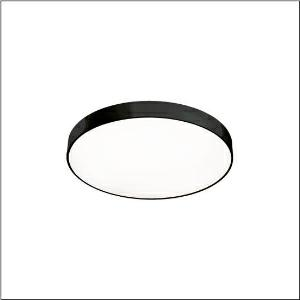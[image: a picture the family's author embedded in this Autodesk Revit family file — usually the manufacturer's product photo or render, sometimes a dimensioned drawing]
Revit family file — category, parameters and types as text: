
# Revit family: round_21_m_51mr36fm8421b
name_source: partatom
category: Lighting Fixtures
units: mm (PartAtom-declared; Revit-internal decimal feet)

## family parameters
Cut with Voids When Loaded = No
Host = Face
Light Source = No
Part Type = Normal
Room Calculation Point = No
Round Connector Dimension = Use Diameter
Shared = No

## types (1)
- --- (1 x LED, 8140 lm, 61.1 W, 4000K)
    Apparent Load = 61 VA
    CIE Flux Codes = 49 80 96 100 100
    Color Rendering = 80
    Color Temperature = 4000K
    Default Elevation = 1800 mm
    Description = Round 21 M, wall and ceiling luminaire, primary optical cover: cover, of PMMA, opal, light emission: direct distribution, primary light characteristic: symmetric, installation type: surface-mounted, suspended mounting, LED, rated luminous flux: 8.140lm, luminous efficacy: 133lm/W, light colour: 840, colour temperature: 4000K, with terminal, 3-pole, mains connection: 230V, AC, 50/60Hz, rated input power: 61W, housing, of aluminium, coated, black, diameter: 600mm, height: 62mm, protection rating (complete): IP40, insulation class (complete): insulation class I (protective earthing), certification: CE, impact resistance: IK04, permissible operating ambient temperature: -10..+35°C, packaging unit: 1 piece
    Height = 87 mm
    Lamp = 1 x LED
    Lamp Light Flux = 8140 lm
    Lamp Power = 61.1 W
    Lamp count = 1
    Length = 600 mm
    Luminous efficacy = 133 lm/W
    Manufacturer = Siteco
    ModVariant = No
    Model = 51MR36FM8421B
    Mounting Place = Ceiling
    Mounting Type = Surface mounted
    Number of Poles = 1
    OnlyDefault = Yes
    Power Factor = 1
    Product Name = Round 21 M
    Product group = wall and ceiling luminaire
    ProductGroupID = 301
    Protection Class = Protection class I
    Protection Degree = IP 40
    RLX_Detail_Level = 1
    RLX_Emergency_Light_Flux = 0 lm
    RLX_Emergency_Type = 0
    RLX_Emergency_Type_DB = No
    RlxData = <blob elided: 20321 chars, md5=0edd09dc>
    Socket = socket
    Standby Power = 0 W
    System Light Flux = 8140 lm
    System Power = 61 W
    Type Comments = factory setting: luminous flux: 100 % | (ON | ON | ON | ON) | 700 mA
    Type Image = l_1258332.jpg
    URL = http://relux.com
    VarID = @adj_013369
    Voltage = 0 V
    Weight = 0.00 kg
    Width = 0 mm  [stored 0 ft]

note: [stored X ft] marks values corroborated as IEEE doubles in the binary element streams (Revit-internal decimal feet)

## geometry (parser evidence)
native form markers: Blend x4, Sweep x9
no freeform markers — native parametric forms only
